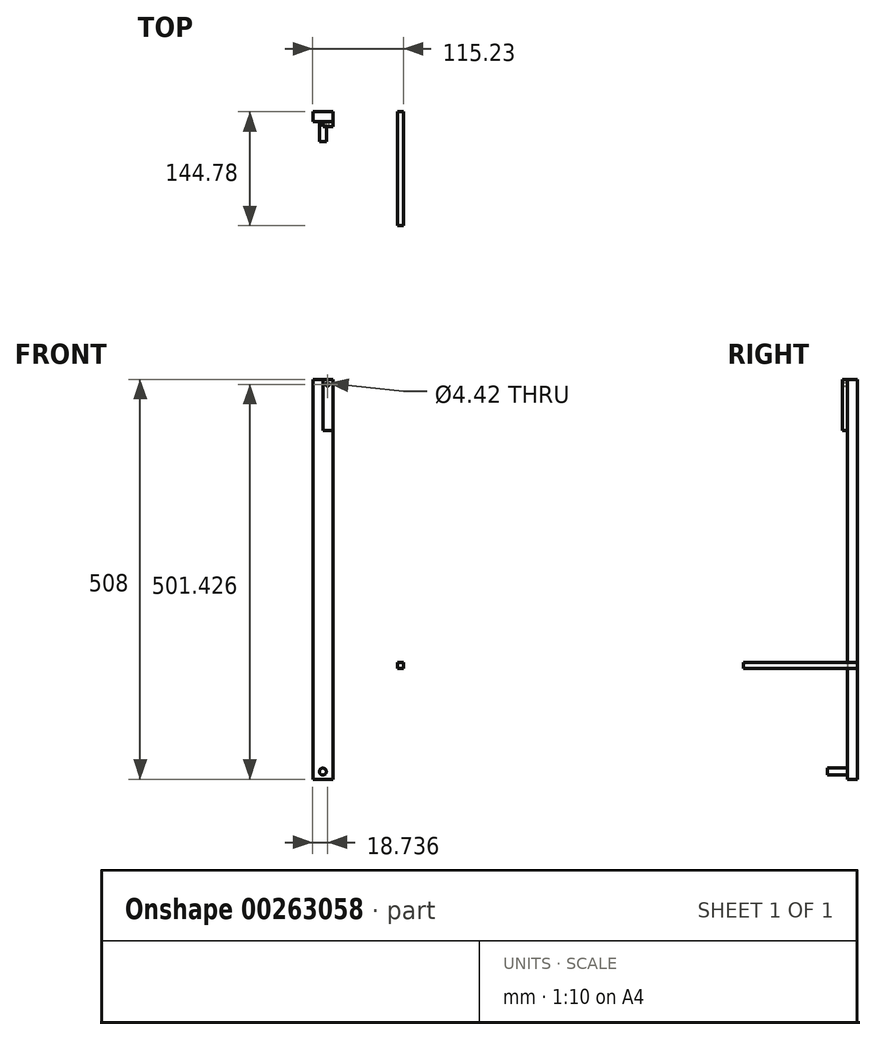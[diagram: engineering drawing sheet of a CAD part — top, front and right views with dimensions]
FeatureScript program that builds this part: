
annotation { "Feature Type Name" : "Feature", "Feature Type Description" : "" }
export const myFeature = defineFeature(function(context is Context, id is Id, definition is map)
    precondition{}
    {
        {
            var Q0;
            Q0=qCreatedBy(makeId("Front.planeOp"),FACE);
            var sketch = newSketch(context, id + "F0", { "sketchPlane" : qUnion([Q0])});
            skLineSegment(sketch, "E0.bottom", {"start": v(-45.45, 298.56) * mm, "end": v(-20.05, 298.56) * mm});
            skLineSegment(sketch, "E0.top", {"start": v(-45.45, -209.44) * mm, "end": v(-20.05, -209.44) * mm});
            skLineSegment(sketch, "E0.left", {"start": v(-45.45, 298.56) * mm, "end": v(-45.45, -209.44) * mm});
            skLineSegment(sketch, "E0.right", {"start": v(-20.05, 298.56) * mm, "end": v(-20.05, -209.44) * mm});
            skSolve(sketch);
        }
        {
            var Q0;
            Q0=makeQuery(id+"F0.imprint","IMPRINT",FACE,{"disambiguationData":[TD([[makeQuery(id+"F0.imprint","IMPRINT",EDGE,{"derivedFrom":sQuery(id+"F0.wireOp",EDGE,"E0.bottom")}),-1.0]])]});
            extrude(context, id + "F1", {"entities" : qUnion([Q0]), "depth" : 12.7 * mm});
        }
        {
            var Q0;
            Q0=makeQuery(id+"F1.opExtrude","CAP_FACE",FACE,{"disambiguationData":[OSD([sQuery(id+"F0.wireOp",EDGE,"E0.bottom"),sQuery(id+"F0.wireOp",EDGE,"E0.top"),sQuery(id+"F0.wireOp",EDGE,"E0.left"),sQuery(id+"F0.wireOp",EDGE,"E0.right")])],"isStart":false});
            var sketch = newSketch(context, id + "F2", { "sketchPlane" : qUnion([Q0])});
            skLineSegment(sketch, "E1.bottom", {"start": v(-32.75, 298.56) * mm, "end": v(-20.05, 298.56) * mm});
            skLineSegment(sketch, "E1.top", {"start": v(-32.75, 233.8) * mm, "end": v(-20.05, 233.8) * mm});
            skLineSegment(sketch, "E1.left", {"start": v(-32.75, 298.56) * mm, "end": v(-32.75, 233.8) * mm});
            skLineSegment(sketch, "E1.right", {"start": v(-20.05, 298.56) * mm, "end": v(-20.05, 233.8) * mm});
            skSolve(sketch);
        }
        {
            var Q0;
            Q0=makeQuery(id+"F2.imprint","IMPRINT",FACE,{"disambiguationData":[TD([[makeQuery(id+"F2.imprint","IMPRINT",EDGE,{"derivedFrom":sQuery(id+"F2.wireOp",EDGE,"E1.bottom")}),-1.0]])]});
            var sketch = newSketch(context, id + "F3", { "sketchPlane" : qUnion([Q0])});
            skCircle(sketch, "E2", {"center": v(-26.71, 291.99) * mm, "radius": 2.21 * mm});
            skSolve(sketch);
        }
        {
            var Q0;
            Q0=makeQuery(id+"F3.imprint","IMPRINT",FACE,{"disambiguationData":[TD([[makeQuery(id+"F3.imprint","IMPRINT",EDGE,{"derivedFrom":sQuery(id+"F3.wireOp",EDGE,"E2")}),-1.0]])]});
            extrude(context, id + "F4", {"entities" : qUnion([Q0]), "depth" : 6.35 * mm});
        }
        {
            var Q0;
            {var subQ4=sQuery(id+"F2.wireOp",EDGE,"E1.top");Q0=makeQuery(id+"F2.imprint","IMPRINT",FACE,{"disambiguationData":[TD([[makeQuery(id+"F2.imprint","IMPRINT",EDGE,{"derivedFrom":subQ4}),-1.0]])]});}
            var sketch = newSketch(context, id + "F5", { "sketchPlane" : qUnion([Q0])});
            skCircle(sketch, "E3", {"center": v(-32.62, -199.78) * mm, "radius": 4.4 * mm});
            skSolve(sketch);
        }
        {
            var Q0;
            Q0=makeQuery(id+"F5.imprint","IMPRINT",FACE,{"disambiguationData":[TD([[makeQuery(id+"F5.imprint","IMPRINT",EDGE,{"derivedFrom":sQuery(id+"F5.wireOp",EDGE,"E3")}),1.0]])]});
            extrude(context, id + "F6", {"entities" : qUnion([Q0]), "depth" : 25.4 * mm});
        }
        {
            var Q0;
            Q0=qCreatedBy(makeId("Front.planeOp"),FACE);
            var sketch = newSketch(context, id + "F7", { "sketchPlane" : qUnion([Q0])});
            skLineSegment(sketch, "E4.bottom", {"start": v(69.78, -61.37) * mm, "end": v(62.05, -61.37) * mm});
            skLineSegment(sketch, "E4.top", {"start": v(69.78, -68.6) * mm, "end": v(62.05, -68.6) * mm});
            skLineSegment(sketch, "E4.left", {"start": v(69.78, -61.37) * mm, "end": v(69.78, -68.6) * mm});
            skLineSegment(sketch, "E4.right", {"start": v(62.05, -61.37) * mm, "end": v(62.05, -68.6) * mm});
            skSolve(sketch);
        }
        {
            var Q0;
            Q0=makeQuery(id+"F7.imprint","IMPRINT",FACE,{"disambiguationData":[TD([[makeQuery(id+"F7.imprint","IMPRINT",EDGE,{"derivedFrom":sQuery(id+"F7.wireOp",EDGE,"E4.bottom")}),1.0]])]});
            extrude(context, id + "F8", {"entities" : qUnion([Q0]), "depth" : 144.78 * mm});
        }
    });
